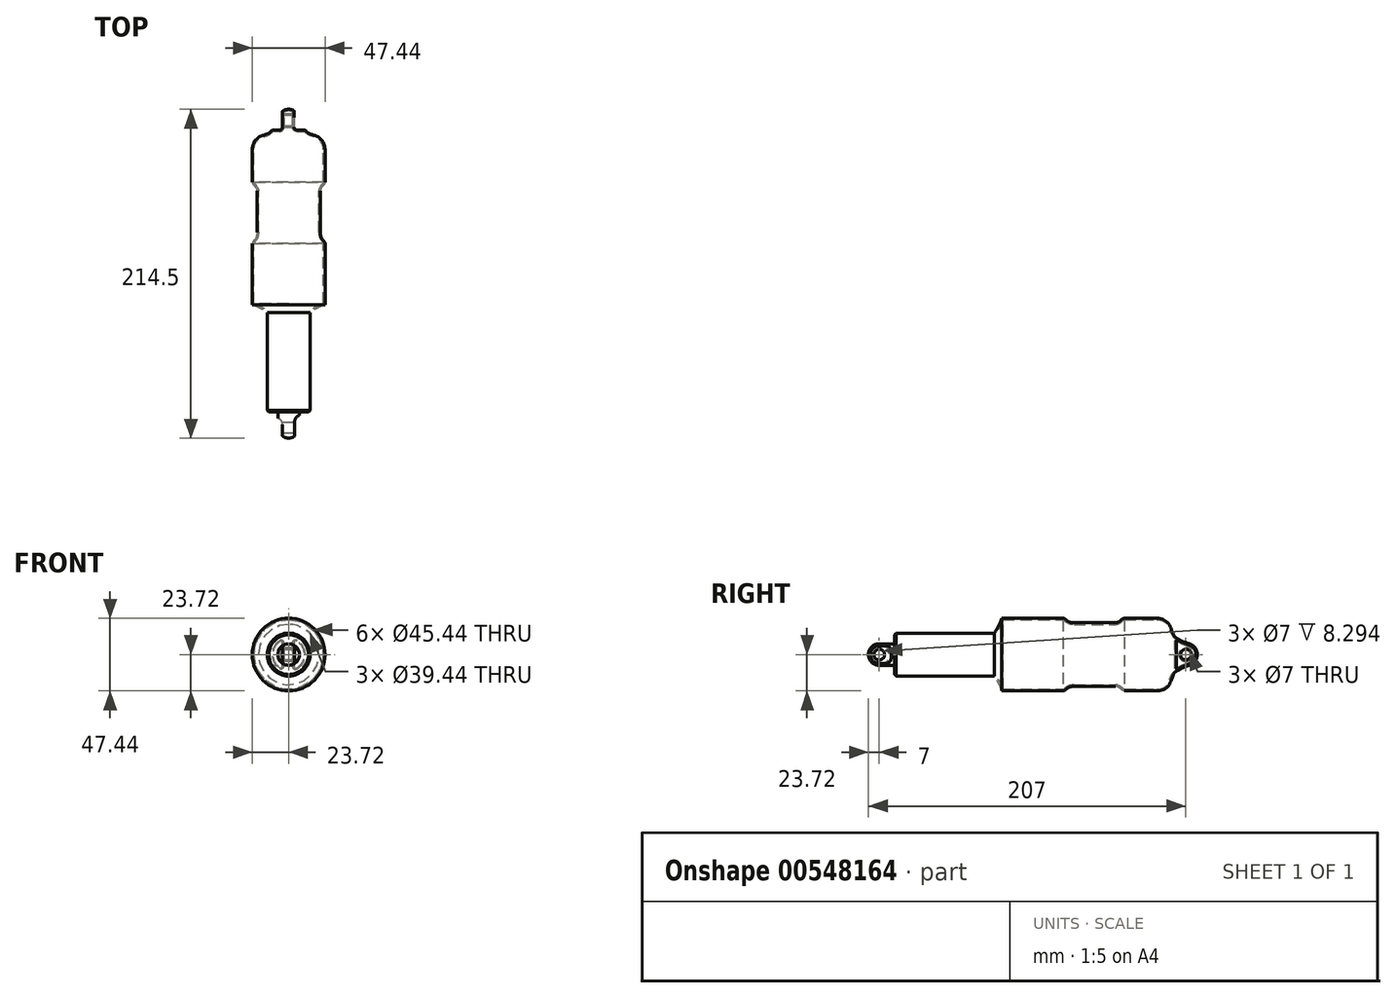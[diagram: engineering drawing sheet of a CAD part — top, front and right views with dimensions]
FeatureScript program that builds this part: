
annotation { "Feature Type Name" : "Feature", "Feature Type Description" : "" }
export const myFeature = defineFeature(function(context is Context, id is Id, definition is map)
    precondition{}
    {
        {
            var Q0;
            Q0=qCreatedBy(makeId("Right.planeOp"),FACE);
            var sketch = newSketch(context, id + "F0", { "sketchPlane" : qUnion([Q0])});
            skLineSegment(sketch, "E0", {"start": v(-120, 23.72) * mm, "end": v(-80, 23.72) * mm});
            skArc(sketch, "E1", {"start": v(7.5, 0) * mm, "mid": v(6.05, 4.43) * mm, "end": v(2.26, 7.15) * mm});
            skLineSegment(sketch, "E2", {"start": v(7.5, 0) * mm, "end": v(-125, 0) * mm});
            skLineSegment(sketch, "E3", {"start": v(-125, 0) * mm, "end": v(-125, 14) * mm});
            skArc(sketch, "E4", {"start": v(-125, 14) * mm, "mid": v(-122.12, 18.66) * mm, "end": v(-120, 23.72) * mm});
            skLineSegment(sketch, "E5", {"start": v(-72.85, 20.72) * mm, "end": v(-45.84, 20.72) * mm});
            skLineSegment(sketch, "E6.trimOffspring", {"start": v(-40, 23.72) * mm, "end": v(-18.81, 23.72) * mm});
            skLineSegment(sketch, "E7", {"start": v(43.2, 0) * mm, "end": v(-134.18, 0) * mm, "construction": true});
            skPoint(sketch, "E8.end.orphan", {"position": v(-40, 23.72) * mm});
            skFitSpline(sketch, "E9", {"points": [v(-45.84, 20.72) * mm, v(-42.63, 22.17) * mm, v(-40, 23.72) * mm], "startDerivative": vector(6.93, 0) * mm, "endDerivative": vector(6.23, 0) * mm});
            skFitSpline(sketch, "E10", {"points": [v(-80, 23.72) * mm, v(-77.4, 22) * mm, v(-72.85, 20.72) * mm], "startDerivative": vector(6.72, 0) * mm, "endDerivative": vector(9.12, 0) * mm});
            skFitSpline(sketch, "E11", {"points": [v(-18.81, 23.72) * mm, v(-11.06, 19.99) * mm, v(-7.49, 12.22) * mm, v(2.26, 7.15) * mm], "startDerivative": vector(29.69, 0) * mm, "endDerivative": vector(32.34, -10.22) * mm});
            skSolve(sketch);
        }
        {
            var Q0;
            Q0 = qSketchRegion(id + "F0", true);
            var Q1;
            Q1=sQuery(id+"F0.wireOp",EDGE,"E7");
            revolve(context, id + "F1", {"entities" : qUnion([Q0]), "axis" : qUnion([Q1]), "revolveType" : RevolveType.FULL});
        }
        {
            var Q0;
            Q0=qCreatedBy(makeId("Top.planeOp"),FACE);
            var sketch = newSketch(context, id + "F2", { "sketchPlane" : qUnion([Q0])});
            skLineSegment(sketch, "E12", {"start": v(-4, 8) * mm, "end": v(-4, -4) * mm});
            skArc(sketch, "E13", {"start": v(-6, -6) * mm, "mid": v(-4.59, -5.41) * mm, "end": v(-4, -4) * mm});
            skLineSegment(sketch, "E14", {"start": v(-6, -6) * mm, "end": v(-14.05, -6) * mm});
            skLineSegment(sketch, "E15", {"start": v(-14.05, -6) * mm, "end": v(-14.05, 8) * mm});
            skLineSegment(sketch, "E16", {"start": v(-14.05, 8) * mm, "end": v(-4, 8) * mm});
            skLineSegment(sketch, "E17.bottom", {"start": v(3.5, 8) * mm, "end": v(13.54, 8) * mm});
            skLineSegment(sketch, "E17.top", {"start": v(5.5, -6) * mm, "end": v(13.54, -6) * mm});
            skLineSegment(sketch, "E17.left", {"start": v(3.5, 8) * mm, "end": v(3.5, -4) * mm});
            skLineSegment(sketch, "E17.right", {"start": v(13.54, 8) * mm, "end": v(13.54, -6) * mm});
            skArc(sketch, "E18", {"start": v(3.5, -4) * mm, "mid": v(4.08, -5.41) * mm, "end": v(5.5, -6) * mm});
            skSolve(sketch);
        }
        {
            var Q0;
            Q0 = qSketchRegion(id + "F2", true);
            var Q1;
            Q1=makeQuery(id+"F1.opRevolve","SWEPT_BODY",BODY,{"disambiguationData":[OSD([sQuery(id+"F0.wireOp",EDGE,"E0"),sQuery(id+"F0.wireOp",EDGE,"E1"),sQuery(id+"F0.wireOp",EDGE,"E2"),sQuery(id+"F0.wireOp",EDGE,"E3"),sQuery(id+"F0.wireOp",EDGE,"E4"),sQuery(id+"F0.wireOp",EDGE,"E5"),sQuery(id+"F0.wireOp",EDGE,"E6.trimOffspring"),sQuery(id+"F0.wireOp",EDGE,"E9"),sQuery(id+"F0.wireOp",EDGE,"E10"),sQuery(id+"F0.wireOp",EDGE,"E11")])]});
            extrude(context, id + "F3", {"entities" : qUnion([Q0]), "operationType" : NewBodyOperationType.REMOVE, "endBound" : BoundingType.THROUGH_ALL, "oppositeDirection" : true, "depth" : 25 * mm, "endBoundEntityBody" : qUnion([Q1]), "offsetDistance" : 25 * mm, "hasSecondDirection" : true, "secondDirectionBound" : SecondDirectionBoundingType.THROUGH_ALL, "secondDirectionOppositeDirection" : false, "secondDirectionDepth" : 25 * mm});
        }
        {
            var Q0;
            Q0=makeQuery(id+"F3.boolean.opBoolean","COPY",FACE,{"derivedFrom":makeQuery(id+"F3.opExtrude","SWEPT_FACE",FACE,{"disambiguationData":[OSD([sQuery(id+"F2.wireOp",EDGE,"E12")])]})});
            var sketch = newSketch(context, id + "F4", { "sketchPlane" : qUnion([Q0])});
            skCircle(sketch, "E19", {"center": v(0, 0) * mm, "radius": 3.5 * mm});
            skSolve(sketch);
        }
        {
            var Q0;
            Q0 = qSketchRegion(id + "F4", true);
            extrude(context, id + "F5", {"entities" : qUnion([Q0]), "operationType" : NewBodyOperationType.REMOVE, "endBound" : BoundingType.THROUGH_ALL, "oppositeDirection" : true, "depth" : 25 * mm, "offsetDistance" : 25 * mm, "hasSecondDirection" : true, "secondDirectionBound" : SecondDirectionBoundingType.THROUGH_ALL, "secondDirectionOppositeDirection" : false, "secondDirectionDepth" : 25 * mm});
        }
        {
            var Q0;
            Q0=makeQuery(id+"F1.opRevolve","SWEPT_FACE",FACE,{"disambiguationData":[OSD([sQuery(id+"F0.wireOp",EDGE,"E3")])]});
            var Q1;
            Q1=makeQuery(id+"F1.opRevolve","SWEPT_BODY",BODY,{"disambiguationData":[OSD([sQuery(id+"F0.wireOp",EDGE,"E0"),sQuery(id+"F0.wireOp",EDGE,"E1"),sQuery(id+"F0.wireOp",EDGE,"E2"),sQuery(id+"F0.wireOp",EDGE,"E3"),sQuery(id+"F0.wireOp",EDGE,"E4"),sQuery(id+"F0.wireOp",EDGE,"E5"),sQuery(id+"F0.wireOp",EDGE,"E6.trimOffspring"),sQuery(id+"F0.wireOp",EDGE,"E9"),sQuery(id+"F0.wireOp",EDGE,"E10"),sQuery(id+"F0.wireOp",EDGE,"E11")])]});
            shell(context, id + "F6", {"entities" : qUnion([Q0]), "parts" : qUnion([Q1]), "thickness" : 1 * mm});
        }
        {
            var Q0;
            Q0=qCreatedBy(makeId("Right.planeOp"),FACE);
            var sketch = newSketch(context, id + "F7", { "sketchPlane" : qUnion([Q0])});
            skLineSegment(sketch, "E20", {"start": v(32.28, 0) * mm, "end": v(-200, 0) * mm, "construction": true});
            skLineSegment(sketch, "E21.bottom", {"start": v(-200, 0) * mm, "end": v(-125, 0) * mm});
            skLineSegment(sketch, "E21.top", {"start": v(-190, 14) * mm, "end": v(-125, 14) * mm});
            skLineSegment(sketch, "E21.right", {"start": v(-125, 0) * mm, "end": v(-125, 14) * mm});
            skLineSegment(sketch, "E22", {"start": v(0, 18.93) * mm, "end": v(0, -37.33) * mm, "construction": true});
            skLineSegment(sketch, "E23", {"start": v(-190, 14) * mm, "end": v(-190, 7) * mm});
            skLineSegment(sketch, "E24", {"start": v(-190, 7) * mm, "end": v(-200, 7) * mm});
            skLineSegment(sketch, "E25", {"start": v(-200, 0) * mm, "end": v(-207, 0) * mm});
            skArc(sketch, "E26", {"start": v(-200, 7) * mm, "mid": v(-204.95, 4.95) * mm, "end": v(-207, 0) * mm});
            skSolve(sketch);
        }
        {
            var Q0;
            Q0 = qSketchRegion(id + "F7", true);
            var Q1;
            Q1=sQuery(id+"F7.wireOp",EDGE,"E20");
            revolve(context, id + "F8", {"entities" : qUnion([Q0]), "axis" : qUnion([Q1]), "revolveType" : RevolveType.FULL});
        }
        {
            var Q0;
            Q0=qCreatedBy(makeId("Top.planeOp"),FACE);
            var sketch = newSketch(context, id + "F9", { "sketchPlane" : qUnion([Q0])});
            skLineSegment(sketch, "E27", {"start": v(-51.4, 0) * mm, "end": v(123.75, 0) * mm, "construction": true});
            skLineSegment(sketch, "E28", {"start": v(0, 55.27) * mm, "end": v(0, -227.86) * mm, "construction": true});
            skLineSegment(sketch, "E29.bottom", {"start": v(4, -210) * mm, "end": v(20, -210) * mm});
            skLineSegment(sketch, "E29.top", {"start": v(8, -192) * mm, "end": v(20, -192) * mm});
            skLineSegment(sketch, "E29.left", {"start": v(4, -210) * mm, "end": v(4, -196) * mm});
            skLineSegment(sketch, "E29.right", {"start": v(20, -210) * mm, "end": v(20, -192) * mm});
            skArc(sketch, "E30", {"start": v(8, -192) * mm, "mid": v(5.17, -193.17) * mm, "end": v(4, -196) * mm});
            skLineSegment(sketch, "E31.bottom", {"start": v(-20, -194) * mm, "end": v(-8, -194) * mm});
            skLineSegment(sketch, "E31.top", {"start": v(-20, -212) * mm, "end": v(-4, -212) * mm});
            skLineSegment(sketch, "E31.left", {"start": v(-20, -194) * mm, "end": v(-20, -212) * mm});
            skLineSegment(sketch, "E31.right", {"start": v(-4, -198) * mm, "end": v(-4, -212) * mm});
            skArc(sketch, "E32", {"start": v(-4, -198) * mm, "mid": v(-5.17, -195.17) * mm, "end": v(-8, -194) * mm});
            skSolve(sketch);
        }
        {
            var Q0;
            Q0 = qSketchRegion(id + "F9", true);
            extrude(context, id + "F10", {"entities" : qUnion([Q0]), "operationType" : NewBodyOperationType.REMOVE, "endBound" : BoundingType.THROUGH_ALL, "oppositeDirection" : true, "depth" : 25 * mm, "offsetDistance" : 25 * mm, "hasSecondDirection" : true, "secondDirectionBound" : SecondDirectionBoundingType.THROUGH_ALL, "secondDirectionOppositeDirection" : false, "secondDirectionDepth" : 25 * mm});
        }
        {
            var Q0;
            Q0=makeQuery(id+"F8.opRevolve","SWEPT_EDGE",EDGE,{"disambiguationData":[OSD([sQuery(id+"F7.wireOp",EDGE,"E21.top"),sQuery(id+"F7.wireOp",EDGE,"E23")])]});
            chamfer(context, id + "F11", {"entities" : qUnion([Q0]), "width" : 1 * mm, "tangentPropagation" : true});
        }
        {
            var Q0;
            Q0=makeQuery(id+"F8.opRevolve","SWEPT_EDGE",EDGE,{"disambiguationData":[OSD([sQuery(id+"F7.wireOp",EDGE,"E23"),sQuery(id+"F7.wireOp",EDGE,"E24")])]});
            fillet(context, id + "F12", {"entities" : qUnion([Q0]), "radius" : 1 * mm, "tangentPropagation" : true, "allowEdgeOverflow" : false});
        }
        {
            var Q0;
            Q0=qCreatedBy(makeId("Right.planeOp"),FACE);
            var sketch = newSketch(context, id + "F13", { "sketchPlane" : qUnion([Q0])});
            skCircle(sketch, "E33", {"center": v(-200, 0) * mm, "radius": 3.5 * mm});
            skSolve(sketch);
        }
        {
            var Q0;
            Q0 = qSketchRegion(id + "F13", true);
            extrude(context, id + "F14", {"entities" : qUnion([Q0]), "operationType" : NewBodyOperationType.REMOVE, "endBound" : BoundingType.THROUGH_ALL, "oppositeDirection" : true, "depth" : 25 * mm, "offsetDistance" : 25 * mm, "hasSecondDirection" : true, "secondDirectionBound" : SecondDirectionBoundingType.THROUGH_ALL, "secondDirectionOppositeDirection" : false, "secondDirectionDepth" : 25 * mm});
        }
    });
